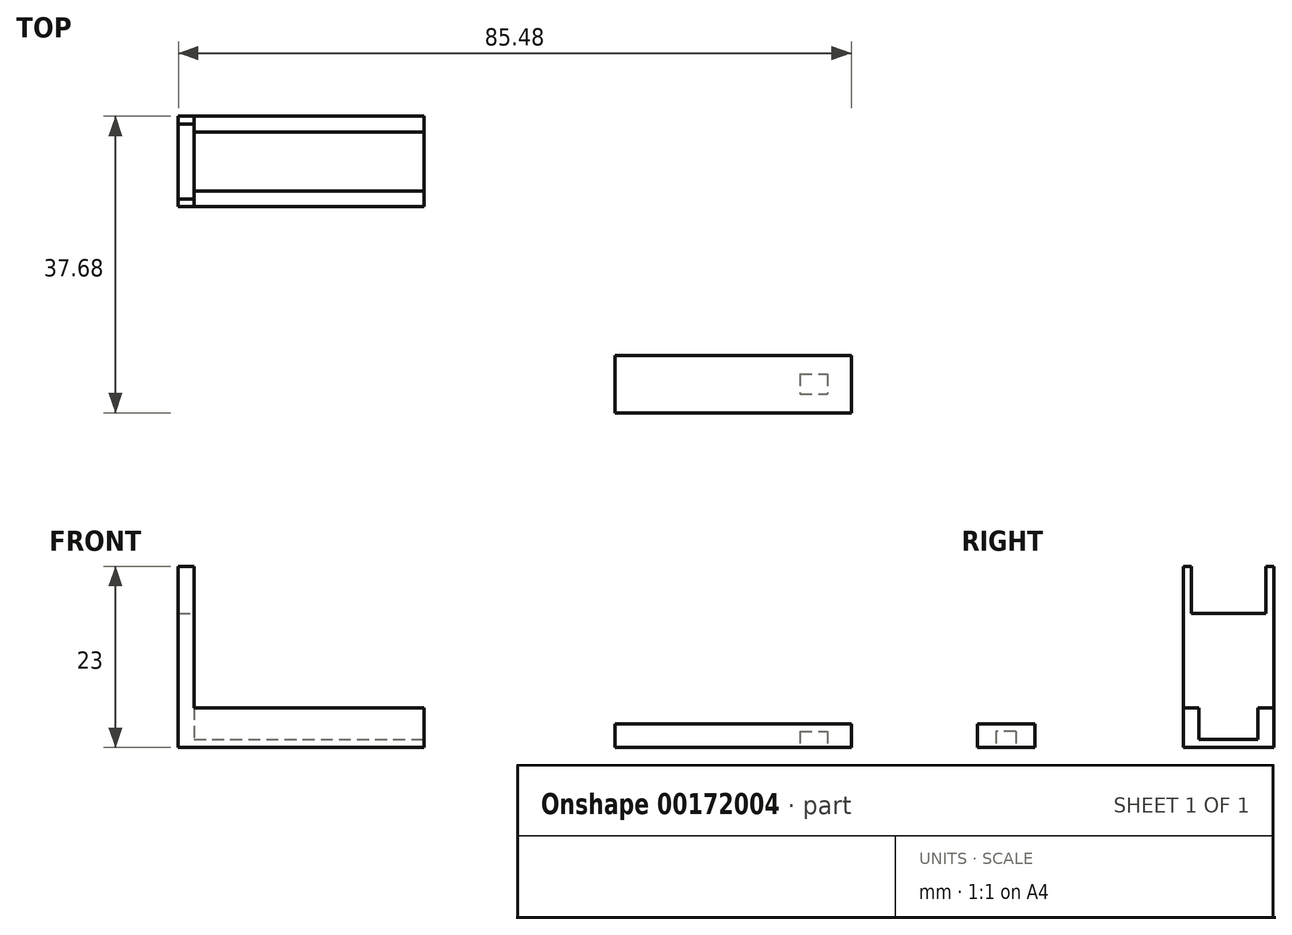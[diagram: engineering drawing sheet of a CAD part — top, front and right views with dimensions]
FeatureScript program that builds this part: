
annotation { "Feature Type Name" : "Feature", "Feature Type Description" : "" }
export const myFeature = defineFeature(function(context is Context, id is Id, definition is map)
    precondition{}
    {
        {
            var Q0;
            Q0=qCreatedBy(makeId("Top.planeOp"),FACE);
            var sketch = newSketch(context, id + "F0", { "sketchPlane" : qUnion([Q0])});
            skLineSegment(sketch, "E0.bottom", {"start": v(-5.9, 2.23) * mm, "end": v(24.1, 2.23) * mm});
            skLineSegment(sketch, "E0.top", {"start": v(-5.9, -5.07) * mm, "end": v(24.1, -5.07) * mm});
            skLineSegment(sketch, "E0.left", {"start": v(-5.9, 2.23) * mm, "end": v(-5.9, -5.07) * mm});
            skLineSegment(sketch, "E0.right", {"start": v(24.1, 2.23) * mm, "end": v(24.1, -5.07) * mm});
            skLineSegment(sketch, "E1.bottom", {"start": v(17.6, -0.17) * mm, "end": v(21.1, -0.17) * mm});
            skLineSegment(sketch, "E1.top", {"start": v(17.6, -2.67) * mm, "end": v(21.1, -2.67) * mm});
            skLineSegment(sketch, "E1.left", {"start": v(17.6, -0.17) * mm, "end": v(17.6, -2.67) * mm});
            skLineSegment(sketch, "E1.right", {"start": v(21.1, -0.17) * mm, "end": v(21.1, -2.67) * mm});
            skLineSegment(sketch, "E2", {"start": v(17.6, -2.67) * mm, "end": v(17.6, -5.07) * mm});
            skLineSegment(sketch, "E3", {"start": v(17.6, -0.17) * mm, "end": v(17.6, 2.23) * mm});
            skSolve(sketch);
        }
        {
            var Q0;
            {var subQ0=sQuery(id+"F0.wireOp",EDGE,"E0.left");Q0=makeQuery(id+"F0.imprint","IMPRINT",FACE,{"disambiguationData":[TD([[makeQuery(id+"F0.imprint","IMPRINT",EDGE,{"derivedFrom":subQ0}),1.0]])]});}
            var Q1;
            {var subQ0=sQuery(id+"F0.wireOp",EDGE,"E0.right");Q1=makeQuery(id+"F0.imprint","IMPRINT",FACE,{"disambiguationData":[TD([[makeQuery(id+"F0.imprint","IMPRINT",EDGE,{"derivedFrom":subQ0}),-1.0]])]});}
            var Q2;
            Q2=makeQuery(id+"F0.imprint","IMPRINT",FACE,{"disambiguationData":[TD([[makeQuery(id+"F0.imprint","IMPRINT",EDGE,{"derivedFrom":sQuery(id+"F0.wireOp",EDGE,"E1.bottom")}),-1.0]])]});
            extrude(context, id + "F1", {"entities" : qUnion([Q0, Q1, Q2]), "depth" : 3 * mm});
        }
        {
            var Q0;
            Q0=makeQuery(id+"F0.imprint","IMPRINT",FACE,{"disambiguationData":[TD([[makeQuery(id+"F0.imprint","IMPRINT",EDGE,{"derivedFrom":sQuery(id+"F0.wireOp",EDGE,"E1.bottom")}),-1.0]])]});
            extrude(context, id + "F2", {"entities" : qUnion([Q0]), "operationType" : NewBodyOperationType.REMOVE, "depth" : 2 * mm});
        }
        {
            var Q0;
            Q0=qCreatedBy(makeId("Top.planeOp"),FACE);
            var sketch = newSketch(context, id + "F3", { "sketchPlane" : qUnion([Q0])});
            skLineSegment(sketch, "E4.bottom", {"start": v(-59.38, 30.6) * mm, "end": v(-30.18, 30.6) * mm});
            skLineSegment(sketch, "E4.top", {"start": v(-59.38, 23.1) * mm, "end": v(-30.18, 23.1) * mm});
            skLineSegment(sketch, "E4.left", {"start": v(-59.38, 30.6) * mm, "end": v(-59.38, 23.1) * mm});
            skLineSegment(sketch, "E4.right", {"start": v(-30.18, 30.6) * mm, "end": v(-30.18, 23.1) * mm});
            skLineSegment(sketch, "E5.bottom", {"start": v(-61.38, 32.6) * mm, "end": v(-28.18, 32.6) * mm});
            skLineSegment(sketch, "E5.top", {"start": v(-61.38, 21.1) * mm, "end": v(-28.18, 21.1) * mm});
            skLineSegment(sketch, "E5.left", {"start": v(-61.38, 32.6) * mm, "end": v(-61.38, 21.1) * mm});
            skLineSegment(sketch, "E5.right", {"start": v(-28.18, 32.6) * mm, "end": v(-28.18, 21.1) * mm});
            skSolve(sketch);
        }
        {
            var Q0;
            Q0=makeQuery(id+"F3.imprint","IMPRINT",FACE,{"disambiguationData":[TD([[makeQuery(id+"F3.imprint","IMPRINT",EDGE,{"derivedFrom":sQuery(id+"F3.wireOp",EDGE,"E4.bottom")}),1.0]])]});
            extrude(context, id + "F4", {"entities" : qUnion([Q0]), "depth" : 5 * mm});
        }
        {
            var Q0;
            Q0=makeQuery(id+"F3.imprint","IMPRINT",FACE,{"disambiguationData":[TD([[makeQuery(id+"F3.imprint","IMPRINT",EDGE,{"derivedFrom":sQuery(id+"F3.wireOp",EDGE,"E4.bottom")}),-1.0]])]});
            extrude(context, id + "F5", {"entities" : qUnion([Q0]), "operationType" : NewBodyOperationType.ADD, "depth" : 1 * mm});
        }
        {
            var Q0;
            Q0=makeQuery(id+"F4.opExtrude","CAP_FACE",FACE,{"disambiguationData":[OSD([sQuery(id+"F3.wireOp",EDGE,"E4.bottom"),sQuery(id+"F3.wireOp",EDGE,"E4.top"),sQuery(id+"F3.wireOp",EDGE,"E4.left"),sQuery(id+"F3.wireOp",EDGE,"E4.right"),sQuery(id+"F3.wireOp",EDGE,"E5.bottom"),sQuery(id+"F3.wireOp",EDGE,"E5.top"),sQuery(id+"F3.wireOp",EDGE,"E5.left"),sQuery(id+"F3.wireOp",EDGE,"E5.right")])],"isStart":false});
            var sketch = newSketch(context, id + "F6", { "sketchPlane" : qUnion([Q0])});
            skLineSegment(sketch, "E6", {"start": v(-59.38, 30.6) * mm, "end": v(-59.38, 32.6) * mm});
            skLineSegment(sketch, "E7", {"start": v(-59.38, 23.1) * mm, "end": v(-59.38, 21.1) * mm});
            skLineSegment(sketch, "E8", {"start": v(-30.18, 30.6) * mm, "end": v(-30.18, 32.6) * mm});
            skLineSegment(sketch, "E9", {"start": v(-30.18, 23.1) * mm, "end": v(-30.18, 21.1) * mm});
            skSolve(sketch);
        }
        {
            var Q0;
            {var subQ2=sQuery(id+"F6.wireOp",EDGE,"E8");Q0=makeQuery(id+"F6.imprint","IMPRINT",FACE,{"disambiguationData":[TD([[makeQuery(id+"F6.imprint","IMPRINT",EDGE,{"derivedFrom":subQ2}),-1.0]])]});}
            extrude(context, id + "F7", {"entities" : qUnion([Q0]), "operationType" : NewBodyOperationType.REMOVE, "oppositeDirection" : true, "depth" : 5 * mm});
        }
        {
            var Q0;
            {var subQ2=sQuery(id+"F6.wireOp",EDGE,"E6");Q0=makeQuery(id+"F6.imprint","IMPRINT",FACE,{"disambiguationData":[TD([[makeQuery(id+"F6.imprint","IMPRINT",EDGE,{"derivedFrom":subQ2}),1.0]])]});}
            extrude(context, id + "F8", {"entities" : qUnion([Q0]), "operationType" : NewBodyOperationType.ADD, "depth" : 12 * mm});
        }
        {
            var Q0;
            Q0=makeQuery(id+"F8.opExtrude","CAP_FACE",FACE,{"disambiguationData":[OSD([sQuery(id+"F3.wireOp",EDGE,"E4.left"),sQuery(id+"F3.wireOp",EDGE,"E5.bottom"),sQuery(id+"F3.wireOp",EDGE,"E5.top"),sQuery(id+"F3.wireOp",EDGE,"E5.left"),sQuery(id+"F6.wireOp",EDGE,"E6"),sQuery(id+"F6.wireOp",EDGE,"E7")])],"isStart":false});
            var sketch = newSketch(context, id + "F9", { "sketchPlane" : qUnion([Q0])});
            skLineSegment(sketch, "E10", {"start": v(-61.38, 22.1) * mm, "end": v(-59.38, 22.1) * mm});
            skLineSegment(sketch, "E11", {"start": v(-61.38, 31.6) * mm, "end": v(-59.38, 31.6) * mm});
            skSolve(sketch);
        }
        {
            var Q0;
            {var subQ0=sQuery(id+"F9.wireOp",EDGE,"E10");Q0=makeQuery(id+"F9.imprint","IMPRINT",FACE,{"disambiguationData":[TD([[makeQuery(id+"F9.imprint","IMPRINT",EDGE,{"derivedFrom":subQ0}),-1.0]])]});}
            var Q1;
            {var subQ0=sQuery(id+"F9.wireOp",EDGE,"E11");Q1=makeQuery(id+"F9.imprint","IMPRINT",FACE,{"disambiguationData":[TD([[makeQuery(id+"F9.imprint","IMPRINT",EDGE,{"derivedFrom":subQ0}),1.0]])]});}
            extrude(context, id + "F10", {"entities" : qUnion([Q0, Q1]), "operationType" : NewBodyOperationType.ADD, "depth" : 6 * mm});
        }
    });
